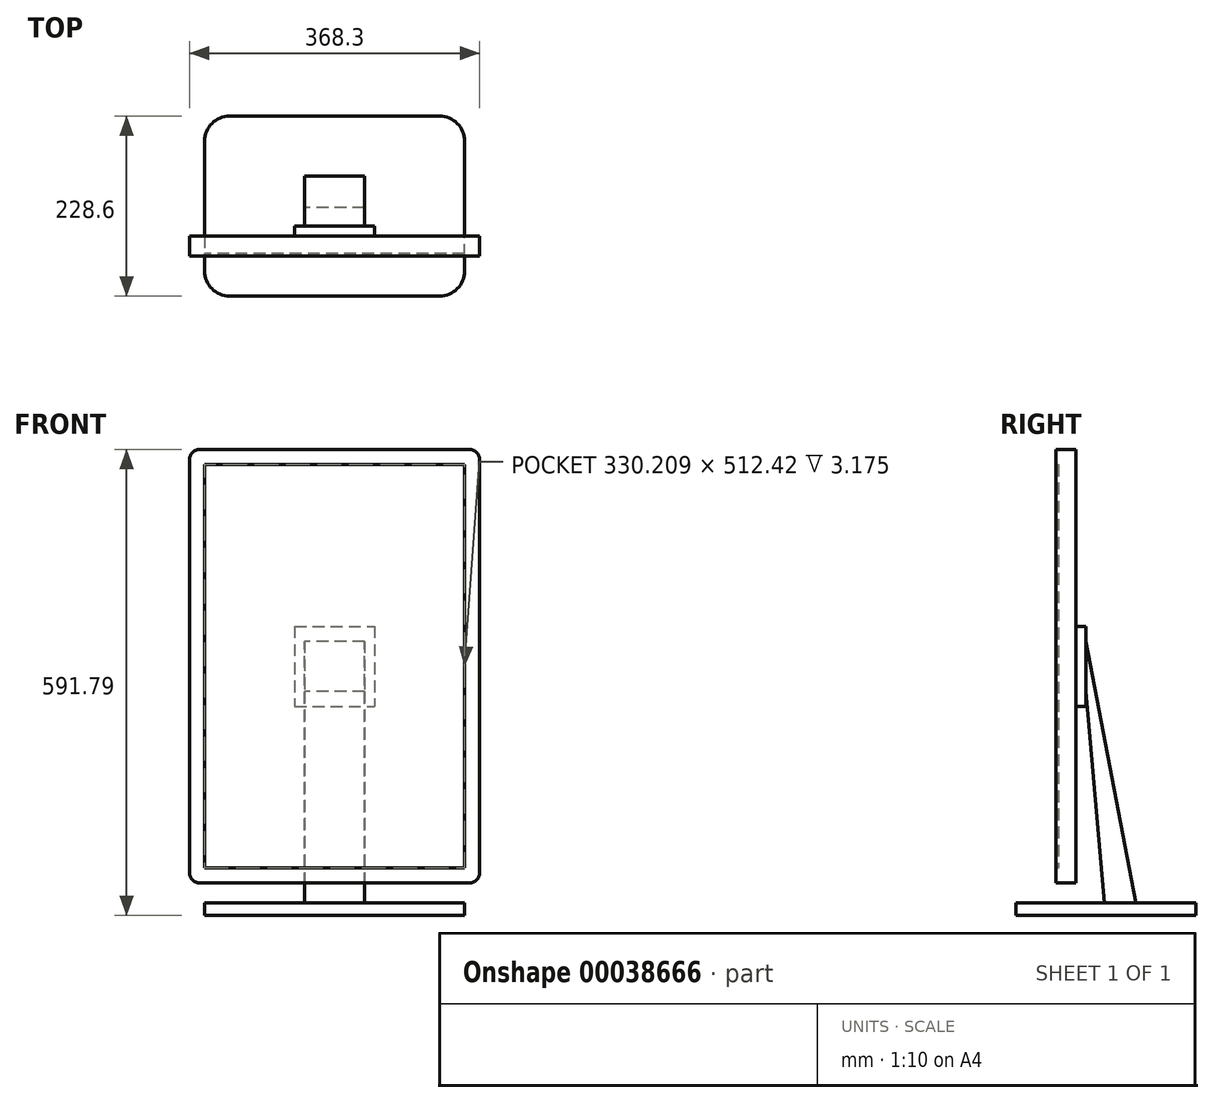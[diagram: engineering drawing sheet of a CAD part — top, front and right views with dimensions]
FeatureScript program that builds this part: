
annotation { "Feature Type Name" : "Feature", "Feature Type Description" : "" }
export const myFeature = defineFeature(function(context is Context, id is Id, definition is map)
    precondition{}
    {
        {
            var Q0;
            Q0=qCreatedBy(makeId("Front.planeOp"),FACE);
            var sketch = newSketch(context, id + "F0", { "sketchPlane" : qUnion([Q0])});
            skLineSegment(sketch, "E0.rect.bottom", {"start": v(165.1, 256.2) * mm, "end": v(-165.1, 256.2) * mm});
            skLineSegment(sketch, "E0.rect.top", {"start": v(165.1, -256.2) * mm, "end": v(-165.1, -256.2) * mm});
            skLineSegment(sketch, "E0.rect.left", {"start": v(165.1, 256.2) * mm, "end": v(165.1, -256.2) * mm});
            skLineSegment(sketch, "E0.rect.right", {"start": v(-165.1, 256.2) * mm, "end": v(-165.1, -256.2) * mm});
            skPoint(sketch, "E0.rect.middle", {"position": v(0, 0) * mm});
            skLineSegment(sketch, "E1", {"start": v(-165.1, 256.2) * mm, "end": v(165.1, -256.2) * mm, "construction": true});
            skLineSegment(sketch, "E2.0", {"start": v(184.15, 262.56) * mm, "end": v(184.15, -262.56) * mm});
            skLineSegment(sketch, "E2.1", {"start": v(171.45, 275.26) * mm, "end": v(-171.45, 275.26) * mm});
            skLineSegment(sketch, "E2.2", {"start": v(-184.15, 262.56) * mm, "end": v(-184.15, -262.56) * mm});
            skLineSegment(sketch, "E2.3", {"start": v(171.45, -275.26) * mm, "end": v(-171.45, -275.26) * mm});
            skPoint(sketch, "E3.visualSharp", {"position": v(-184.15, 275.26) * mm});
            skArc(sketch, "E3.filletArc", {"start": v(-171.45, 275.26) * mm, "mid": v(-180.44, 271.54) * mm, "end": v(-184.15, 262.56) * mm});
            skPoint(sketch, "E4.visualSharp", {"position": v(184.15, 275.26) * mm});
            skArc(sketch, "E4.filletArc", {"start": v(184.15, 262.56) * mm, "mid": v(180.44, 271.54) * mm, "end": v(171.45, 275.26) * mm});
            skPoint(sketch, "E5.visualSharp", {"position": v(184.15, -275.26) * mm});
            skArc(sketch, "E5.filletArc", {"start": v(171.45, -275.26) * mm, "mid": v(180.44, -271.54) * mm, "end": v(184.15, -262.56) * mm});
            skPoint(sketch, "E6.visualSharp", {"position": v(-184.15, -275.26) * mm});
            skArc(sketch, "E6.filletArc", {"start": v(-184.15, -262.56) * mm, "mid": v(-180.44, -271.54) * mm, "end": v(-171.45, -275.26) * mm});
            skSolve(sketch);
        }
        {
            var Q0;
            Q0=makeQuery(id+"F0.imprint","IMPRINT",FACE,{"disambiguationData":[TD([[makeQuery(id+"F0.imprint","IMPRINT",EDGE,{"derivedFrom":sQuery(id+"F0.wireOp",EDGE,"E0.rect.bottom")}),-1.0]])]});
            extrude(context, id + "F1", {"entities" : qUnion([Q0]), "depth" : 25.4 * mm});
        }
        {
            var Q0;
            Q0=makeQuery(id+"F0.imprint","IMPRINT",FACE,{"disambiguationData":[TD([[makeQuery(id+"F0.imprint","IMPRINT",EDGE,{"derivedFrom":sQuery(id+"F0.wireOp",EDGE,"E0.rect.bottom")}),1.0]])]});
            var Q1;
            Q1=sQuery(id+"F0.wireOp",EDGE,"E0.rect.bottom");
            var Q2;
            Q2=sQuery(id+"F0.wireOp",EDGE,"E0.rect.right");
            var Q3;
            Q3=sQuery(id+"F0.wireOp",EDGE,"E0.rect.top");
            var Q4;
            Q4=sQuery(id+"F0.wireOp",EDGE,"E0.rect.left");
            extrude(context, id + "F2", {"entities" : qUnion([Q0]), "operationType" : NewBodyOperationType.ADD, "surfaceEntities" : qUnion([Q1, Q2, Q3, Q4]), "depth" : 22.22 * mm});
        }
        {
            var Q0;
            Q0=makeQuery(id+"F0.imprint","IMPRINT",FACE,{"disambiguationData":[TD([[makeQuery(id+"F0.imprint","IMPRINT",EDGE,{"derivedFrom":sQuery(id+"F0.wireOp",EDGE,"E0.rect.bottom")}),1.0]])]});
            var sketch = newSketch(context, id + "F3", { "sketchPlane" : qUnion([Q0])});
            skLineSegment(sketch, "E7.rect.bottom", {"start": v(-50.8, 50.8) * mm, "end": v(50.8, 50.8) * mm});
            skLineSegment(sketch, "E7.rect.top", {"start": v(-50.8, -50.8) * mm, "end": v(50.8, -50.8) * mm});
            skLineSegment(sketch, "E7.rect.left", {"start": v(-50.8, 50.8) * mm, "end": v(-50.8, -50.8) * mm});
            skLineSegment(sketch, "E7.rect.right", {"start": v(50.8, 50.8) * mm, "end": v(50.8, -50.8) * mm});
            skPoint(sketch, "E7.rect.middle", {"position": v(0, 0) * mm});
            skSolve(sketch);
        }
        {
            var Q0;
            Q0=qSketchRegion(id+"F3",true);
            extrude(context, id + "F4", {"entities" : qUnion([Q0]), "operationType" : NewBodyOperationType.ADD, "oppositeDirection" : true, "depth" : 12.7 * mm});
        }
        {
            var Q0;
            Q0=qCreatedBy(makeId("Right.planeOp"),FACE);
            var sketch = newSketch(context, id + "F5", { "sketchPlane" : qUnion([Q0])});
            skLineSegment(sketch, "E8", {"start": v(12.7, -31.75) * mm, "end": v(36.23, -300.66) * mm});
            skLineSegment(sketch, "E9", {"start": v(36.23, -300.66) * mm, "end": v(-76.2, -300.66) * mm});
            skLineSegment(sketch, "E10", {"start": v(-76.2, -300.66) * mm, "end": v(-76.2, -316.53) * mm});
            skLineSegment(sketch, "E11", {"start": v(-76.2, -316.53) * mm, "end": v(152.4, -316.53) * mm});
            skLineSegment(sketch, "E12", {"start": v(152.4, -316.53) * mm, "end": v(152.4, -300.66) * mm});
            skLineSegment(sketch, "E13", {"start": v(152.4, -300.66) * mm, "end": v(76.2, -300.66) * mm});
            skLineSegment(sketch, "E14", {"start": v(76.2, -300.66) * mm, "end": v(12.7, 31.75) * mm});
            skLineSegment(sketch, "E15", {"start": v(12.7, 31.75) * mm, "end": v(12.7, -31.75) * mm});
            skSolve(sketch);
        }
        {
            var Q0;
            Q0=qSketchRegion(id+"F5",true);
            extrude(context, id + "F6", {"entities" : qUnion([Q0]), "operationType" : NewBodyOperationType.ADD, "endBound" : BoundingType.SYMMETRIC, "depth" : 76.2 * mm});
        }
        {
            var Q0;
            Q0=makeQuery(id+"F6.opExtrude","CAP_FACE",FACE,{"disambiguationData":[OSD([sQuery(id+"F5.wireOp",EDGE,"E8"),sQuery(id+"F5.wireOp",EDGE,"E9"),sQuery(id+"F5.wireOp",EDGE,"E10"),sQuery(id+"F5.wireOp",EDGE,"E11"),sQuery(id+"F5.wireOp",EDGE,"E12"),sQuery(id+"F5.wireOp",EDGE,"E13"),sQuery(id+"F5.wireOp",EDGE,"E14"),sQuery(id+"F5.wireOp",EDGE,"E15")])],"isStart":false});
            var sketch = newSketch(context, id + "F7", { "sketchPlane" : qUnion([Q0])});
            skLineSegment(sketch, "E16.bottom", {"start": v(-76.2, -300.66) * mm, "end": v(152.4, -300.66) * mm});
            skLineSegment(sketch, "E16.top", {"start": v(-76.2, -316.53) * mm, "end": v(152.4, -316.53) * mm});
            skLineSegment(sketch, "E16.left", {"start": v(-76.2, -300.66) * mm, "end": v(-76.2, -316.53) * mm});
            skLineSegment(sketch, "E16.right", {"start": v(152.4, -300.66) * mm, "end": v(152.4, -316.53) * mm});
            skSolve(sketch);
        }
        {
            var Q0;
            Q0=qSketchRegion(id+"F7",true);
            extrude(context, id + "F8", {"entities" : qUnion([Q0]), "operationType" : NewBodyOperationType.ADD, "depth" : 127 * mm});
        }
        {
            var Q0;
            Q0=makeQuery(id+"F6.opExtrude","CAP_FACE",FACE,{"disambiguationData":[OSD([sQuery(id+"F5.wireOp",EDGE,"E8"),sQuery(id+"F5.wireOp",EDGE,"E9"),sQuery(id+"F5.wireOp",EDGE,"E10"),sQuery(id+"F5.wireOp",EDGE,"E11"),sQuery(id+"F5.wireOp",EDGE,"E12"),sQuery(id+"F5.wireOp",EDGE,"E13"),sQuery(id+"F5.wireOp",EDGE,"E14"),sQuery(id+"F5.wireOp",EDGE,"E15")])],"isStart":true});
            var sketch = newSketch(context, id + "F9", { "sketchPlane" : qUnion([Q0])});
            skLineSegment(sketch, "E17.bottom", {"start": v(-152.4, -300.66) * mm, "end": v(76.2, -300.66) * mm});
            skLineSegment(sketch, "E17.top", {"start": v(-152.4, -316.53) * mm, "end": v(76.2, -316.53) * mm});
            skLineSegment(sketch, "E17.left", {"start": v(-152.4, -300.66) * mm, "end": v(-152.4, -316.53) * mm});
            skLineSegment(sketch, "E17.right", {"start": v(76.2, -300.66) * mm, "end": v(76.2, -316.53) * mm});
            skSolve(sketch);
        }
        {
            var Q0;
            Q0=qSketchRegion(id+"F9",true);
            extrude(context, id + "F10", {"entities" : qUnion([Q0]), "operationType" : NewBodyOperationType.ADD, "depth" : 127 * mm});
        }
        {
            var Q0;
            Q0=makeQuery(id+"F10.opExtrude","CAP_EDGE",EDGE,{"disambiguationData":[OSD([sQuery(id+"F9.wireOp",EDGE,"E17.left")])],"isStart":false});
            var Q1;
            Q1=makeQuery(id+"F8.opExtrude","CAP_EDGE",EDGE,{"disambiguationData":[OSD([sQuery(id+"F7.wireOp",EDGE,"E16.right")])],"isStart":false});
            var Q2;
            Q2=makeQuery(id+"F8.opExtrude","CAP_EDGE",EDGE,{"disambiguationData":[OSD([sQuery(id+"F7.wireOp",EDGE,"E16.left")])],"isStart":false});
            var Q3;
            Q3=makeQuery(id+"F10.opExtrude","CAP_EDGE",EDGE,{"disambiguationData":[OSD([sQuery(id+"F9.wireOp",EDGE,"E17.right")])],"isStart":false});
            fillet(context, id + "F11", {"entities" : qUnion([Q0, Q1, Q2, Q3]), "radius" : 31.75 * mm, "tangentPropagation" : true, "allowEdgeOverflow" : false});
        }
    });
